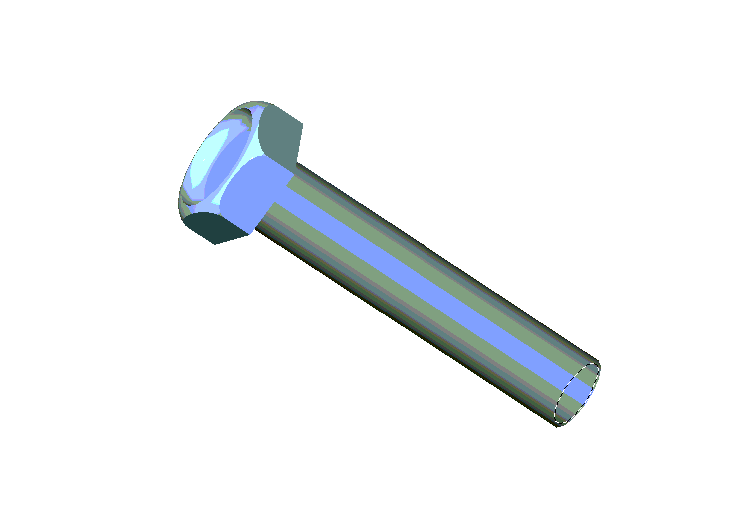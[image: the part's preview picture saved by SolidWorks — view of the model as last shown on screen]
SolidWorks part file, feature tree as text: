
SOLIDWORKS PART (.sldprt)
format: sldprt  version: not decoded by parser v0  size: 199,680 bytes
history: native  units: mm
features: sketch x5, plane x3, extrude x2, cut_revolve x2, fillet x2, material x1, cut_extrude x1, thread x1 + 2 further entries (+7 scaffold rows collapsed)
feature tree (26):
  scaffold x7  (default folders/planes/origin — collapsed)
  material  "Matériau <non spécifié>"
  "Corps de surface"
  plane  "Plane1"
  plane  "Plane2"
  plane  "Plane3"
  "Famille de pièces"
  sketch  "Head Sketch"  dims[D1=60.0deg D2=60.0deg Width across flats=13.0mm]
  extrude  "Head"  Depth=5.3mm Head height=5.3mm
  sketch  "Shank Sketch"  dims[Shank diameter=8.0mm]
  extrude  "Shank"  Depth=40mm Shank length=40mm
  sketch  "Sketch5"  dims[D1=2.0mm]
  cut_revolve  "Head Trim"  Angle=360deg
  sketch  "Sketch6"  dims[D1=11.375mm D2=1.0mm]
  cut_extrude  "Head Cut"  Depth=1.5mm
  fillet  "Fillet1"  Radius=2mm
  fillet  "Fillet2"  Radius=0.5mm
  sketch  "Thread End"  dims[c1.D1=1.0mm c1.D2=1.1mm c2.D1=0.05mm c2.Length of thread=22.0mm]
  cut_revolve  "Thread Cut"  [1 undecoded]
  thread  "Cosmetic Thread2"  Diameter=7mm  [1 undecoded]
decode coverage: 12 of 13 modeling features carry decoded parameters; 2 rows unclassified (native names shown)
note: 2 parameter values undecoded
note: suppression state not decoded; provenance and decode notes live in map.json
